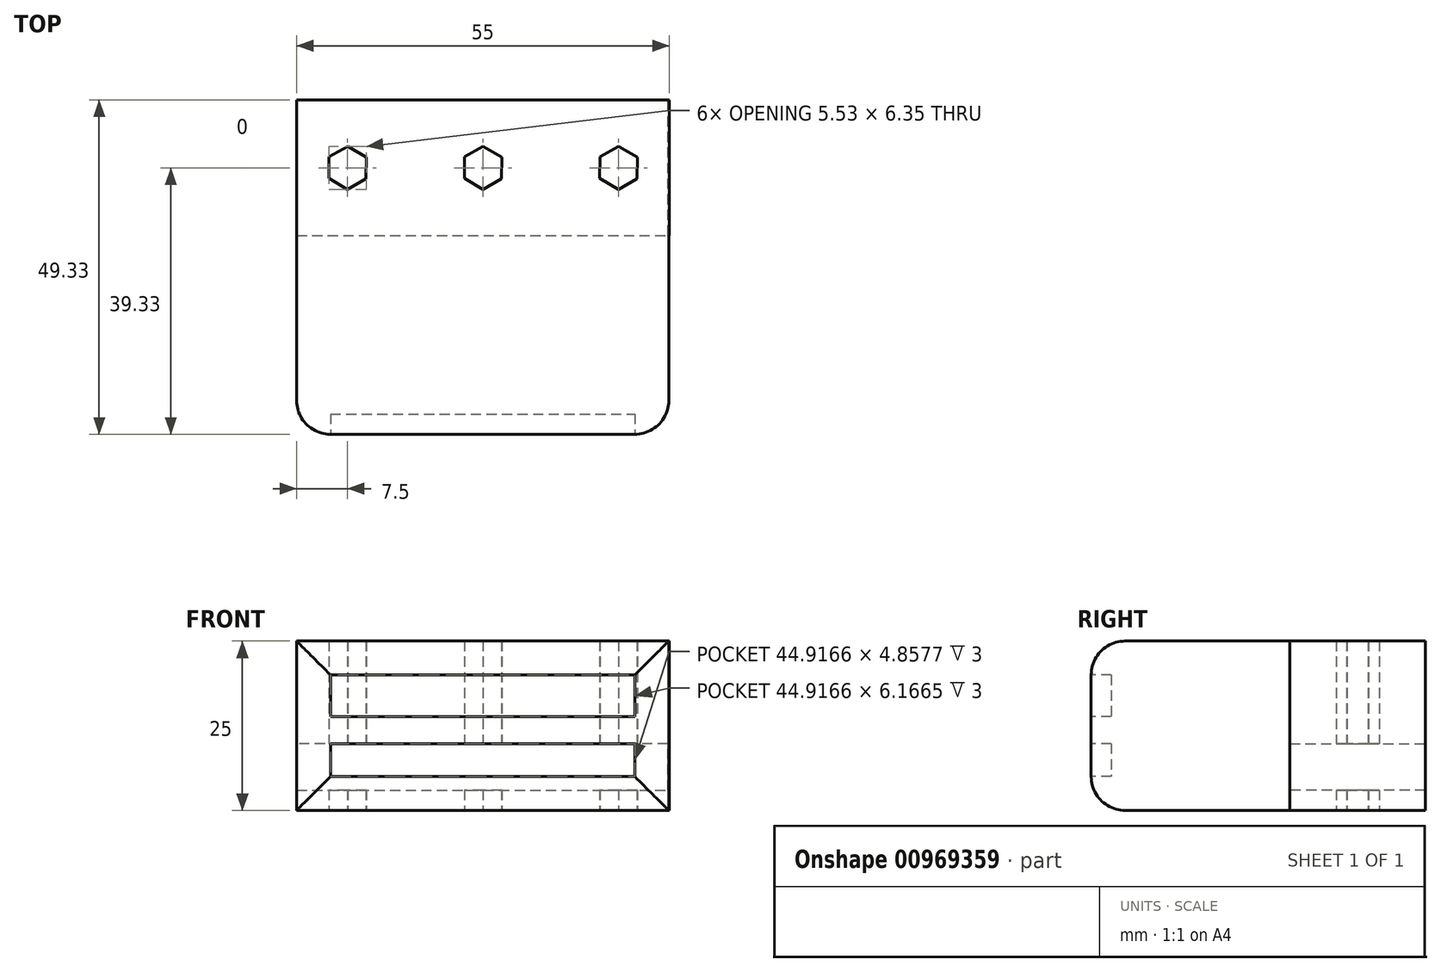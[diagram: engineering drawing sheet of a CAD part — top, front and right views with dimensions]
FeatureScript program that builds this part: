
annotation { "Feature Type Name" : "Feature", "Feature Type Description" : "" }
export const myFeature = defineFeature(function(context is Context, id is Id, definition is map)
    precondition{}
    {
        {
            var Q0;
            Q0=qCreatedBy(makeId("Top.planeOp"),FACE);
            var sketch = newSketch(context, id + "F0", { "sketchPlane" : qUnion([Q0])});
            skPoint(sketch, "E0.middle", {"position": v(0, 0) * mm});
            skCircle(sketch, "E1.cCircle", {"center": v(-20, 0) * mm, "radius": 2.75 * mm, "construction": true});
            skLineSegment(sketch, "E1.0", {"start": v(-22.74, 1.61) * mm, "end": v(-19.97, 3.18) * mm});
            skLineSegment(sketch, "E1.1", {"start": v(-19.97, 3.18) * mm, "end": v(-17.24, 1.56) * mm});
            skLineSegment(sketch, "E1.2", {"start": v(-17.24, 1.56) * mm, "end": v(-17.26, -1.61) * mm});
            skLineSegment(sketch, "E1.3", {"start": v(-17.26, -1.61) * mm, "end": v(-20.03, -3.18) * mm});
            skLineSegment(sketch, "E1.4", {"start": v(-20.03, -3.18) * mm, "end": v(-22.76, -1.56) * mm});
            skLineSegment(sketch, "E1.5", {"start": v(-22.76, -1.56) * mm, "end": v(-22.74, 1.61) * mm});
            skPoint(sketch, "E1.0.midPoint", {"position": v(-21.35, 2.4) * mm});
            skCircle(sketch, "E2", {"center": v(-20, 0) * mm, "radius": 1.75 * mm});
            skCircle(sketch, "E3.1.0.0", {"center": v(0, 0) * mm, "radius": 2.75 * mm, "construction": true});
            skLineSegment(sketch, "E3.1.0.1", {"start": v(2.74, -1.61) * mm, "end": v(-0.03, -3.18) * mm});
            skLineSegment(sketch, "E3.1.0.2", {"start": v(-0.03, -3.18) * mm, "end": v(-2.76, -1.56) * mm});
            skLineSegment(sketch, "E3.1.0.3", {"start": v(-2.76, -1.56) * mm, "end": v(-2.74, 1.61) * mm});
            skLineSegment(sketch, "E3.1.0.4", {"start": v(-2.74, 1.61) * mm, "end": v(0.03, 3.18) * mm});
            skLineSegment(sketch, "E3.1.0.5", {"start": v(0.03, 3.18) * mm, "end": v(2.76, 1.56) * mm});
            skLineSegment(sketch, "E3.1.0.6", {"start": v(2.76, 1.56) * mm, "end": v(2.74, -1.61) * mm});
            skCircle(sketch, "E3.1.0.7", {"center": v(0, 0) * mm, "radius": 1.75 * mm});
            skCircle(sketch, "E3.2.0.0", {"center": v(20, 0) * mm, "radius": 2.75 * mm, "construction": true});
            skLineSegment(sketch, "E3.2.0.1", {"start": v(22.74, -1.61) * mm, "end": v(19.97, -3.18) * mm});
            skLineSegment(sketch, "E3.2.0.2", {"start": v(19.97, -3.18) * mm, "end": v(17.24, -1.56) * mm});
            skLineSegment(sketch, "E3.2.0.3", {"start": v(17.24, -1.56) * mm, "end": v(17.26, 1.61) * mm});
            skLineSegment(sketch, "E3.2.0.4", {"start": v(17.26, 1.61) * mm, "end": v(20.03, 3.18) * mm});
            skLineSegment(sketch, "E3.2.0.5", {"start": v(20.03, 3.18) * mm, "end": v(22.76, 1.56) * mm});
            skLineSegment(sketch, "E3.2.0.6", {"start": v(22.76, 1.56) * mm, "end": v(22.74, -1.61) * mm});
            skCircle(sketch, "E3.2.0.7", {"center": v(20, 0) * mm, "radius": 1.75 * mm});
            skLineSegment(sketch, "E3.direction1", {"start": v(-20, 0) * mm, "end": v(0, 0) * mm, "construction": true});
            skLineSegment(sketch, "E4.bottom", {"start": v(-27.5, 10) * mm, "end": v(27.5, 10) * mm});
            skLineSegment(sketch, "E4.top", {"start": v(-27.5, -10) * mm, "end": v(27.5, -10) * mm});
            skLineSegment(sketch, "E4.left", {"start": v(-27.5, 10) * mm, "end": v(-27.5, -10) * mm});
            skLineSegment(sketch, "E4.right", {"start": v(27.5, 10) * mm, "end": v(27.5, -10) * mm});
            skLineSegment(sketch, "E5.bottom", {"start": v(-27.5, -10) * mm, "end": v(27.42, -10) * mm});
            skLineSegment(sketch, "E5.top", {"start": v(-27.5, -39.33) * mm, "end": v(27.42, -39.33) * mm});
            skLineSegment(sketch, "E5.left", {"start": v(-27.5, -10) * mm, "end": v(-27.5, -39.33) * mm});
            skLineSegment(sketch, "E5.right", {"start": v(27.42, -10) * mm, "end": v(27.42, -39.33) * mm});
            skSolve(sketch);
        }
        {
            var Q0;
            Q0=makeQuery(id+"F0.imprint","IMPRINT",FACE,{"disambiguationData":[TD([[makeQuery(id+"F0.imprint","IMPRINT",EDGE,{"derivedFrom":sQuery(id+"F0.wireOp",EDGE,"E5.top")}),1.0]])]});
            var Q1;
            Q1=makeQuery(id+"F0.imprint","IMPRINT",FACE,{"disambiguationData":[TD([[makeQuery(id+"F0.imprint","IMPRINT",EDGE,{"derivedFrom":sQuery(id+"F0.wireOp",EDGE,"E1.0")}),1.0]])]});
            extrude(context, id + "F1", {"entities" : qUnion([Q0, Q1]), "depth" : 25 * mm, "offsetDistance" : 25 * mm});
        }
        {
            var Q0;
            Q0=qCreatedBy(makeId("Front.planeOp"),FACE);
            var sketch = newSketch(context, id + "F2", { "sketchPlane" : qUnion([Q0])});
            skLineSegment(sketch, "E6.bottom", {"start": v(27.27, 0) * mm, "end": v(-27.53, 0) * mm});
            skLineSegment(sketch, "E6.top", {"start": v(27.27, 9.87) * mm, "end": v(-27.53, 9.87) * mm});
            skLineSegment(sketch, "E6.left", {"start": v(27.27, 0) * mm, "end": v(27.27, 9.87) * mm});
            skLineSegment(sketch, "E6.right", {"start": v(-27.53, 0) * mm, "end": v(-27.53, 9.87) * mm});
            skSolve(sketch);
        }
        {
            var Q0;
            Q0 = qSketchRegion(id + "F2", true);
            extrude(context, id + "F3", {"entities" : qUnion([Q0]), "operationType" : NewBodyOperationType.REMOVE, "depth" : 10 * mm, "offsetDistance" : 25 * mm, "hasSecondDirection" : true, "secondDirectionOppositeDirection" : true, "secondDirectionDepth" : 25 * mm});
        }
        {
            var Q0;
            Q0=makeQuery(id+"F0.imprint","IMPRINT",FACE,{"disambiguationData":[TD([[makeQuery(id+"F0.imprint","IMPRINT",EDGE,{"derivedFrom":sQuery(id+"F0.wireOp",EDGE,"E1.0")}),1.0]])]});
            extrude(context, id + "F4", {"entities" : qUnion([Q0]), "operationType" : NewBodyOperationType.ADD, "depth" : 3 * mm, "offsetDistance" : 25 * mm});
        }
        {
            var Q0;
            Q0=makeQuery(id+"F1.opExtrude","CAP_EDGE",EDGE,{"disambiguationData":[OSD([sQuery(id+"F0.wireOp",EDGE,"E5.top")])],"isStart":false});
            var Q1;
            Q1=makeQuery(id+"F1.opExtrude","CAP_EDGE",EDGE,{"disambiguationData":[OSD([sQuery(id+"F0.wireOp",EDGE,"E5.top")])],"isStart":true});
            var Q2;
            Q2=makeQuery(id+"F1.opExtrude","SWEPT_EDGE",EDGE,{"disambiguationData":[OSD([sQuery(id+"F0.wireOp",EDGE,"E5.top"),sQuery(id+"F0.wireOp",EDGE,"E5.right")])]});
            var Q3;
            Q3=makeQuery(id+"F1.opExtrude","SWEPT_EDGE",EDGE,{"disambiguationData":[OSD([sQuery(id+"F0.wireOp",EDGE,"E5.top"),sQuery(id+"F0.wireOp",EDGE,"E5.left")])]});
            fillet(context, id + "F5", {"entities" : qUnion([Q0, Q1, Q2, Q3]), "radius" : 5 * mm, "tangentPropagation" : true, "allowEdgeOverflow" : false});
        }
        {
            var Q0;
            Q0=makeQuery(id+"F1.opExtrude","SWEPT_FACE",FACE,{"disambiguationData":[OSD([sQuery(id+"F0.wireOp",EDGE,"E5.top")])]});
            var sketch = newSketch(context, id + "F6", { "sketchPlane" : qUnion([Q0])});
            skLineSegment(sketch, "E7.bottom", {"start": v(-22.5, 20) * mm, "end": v(22.42, 20) * mm});
            skLineSegment(sketch, "E7.top", {"start": v(-22.5, 13.83) * mm, "end": v(22.42, 13.83) * mm});
            skLineSegment(sketch, "E7.left", {"start": v(-22.5, 20) * mm, "end": v(-22.5, 13.83) * mm});
            skLineSegment(sketch, "E7.right", {"start": v(22.42, 20) * mm, "end": v(22.42, 13.83) * mm});
            skLineSegment(sketch, "E8.bottom", {"start": v(-22.5, 5) * mm, "end": v(22.42, 5) * mm});
            skLineSegment(sketch, "E8.top", {"start": v(-22.5, 9.86) * mm, "end": v(22.42, 9.86) * mm});
            skLineSegment(sketch, "E8.left", {"start": v(-22.5, 5) * mm, "end": v(-22.5, 9.86) * mm});
            skLineSegment(sketch, "E8.right", {"start": v(22.42, 5) * mm, "end": v(22.42, 9.86) * mm});
            skSolve(sketch);
        }
        {
            var Q0;
            Q0=makeQuery(id+"F6.imprint","IMPRINT",FACE,{"disambiguationData":[TD([[makeQuery(id+"F6.imprint","IMPRINT",EDGE,{"derivedFrom":sQuery(id+"F6.wireOp",EDGE,"E7.bottom")}),1.0]])]});
            var Q1;
            Q1=makeQuery(id+"F6.imprint","IMPRINT",FACE,{"disambiguationData":[TD([[makeQuery(id+"F6.imprint","IMPRINT",EDGE,{"derivedFrom":sQuery(id+"F6.wireOp",EDGE,"E8.bottom")}),1.0]])]});
            extrude(context, id + "F7", {"entities" : qUnion([Q0, Q1]), "operationType" : NewBodyOperationType.REMOVE, "oppositeDirection" : true, "depth" : 3 * mm, "offsetDistance" : 25 * mm});
        }
    });
